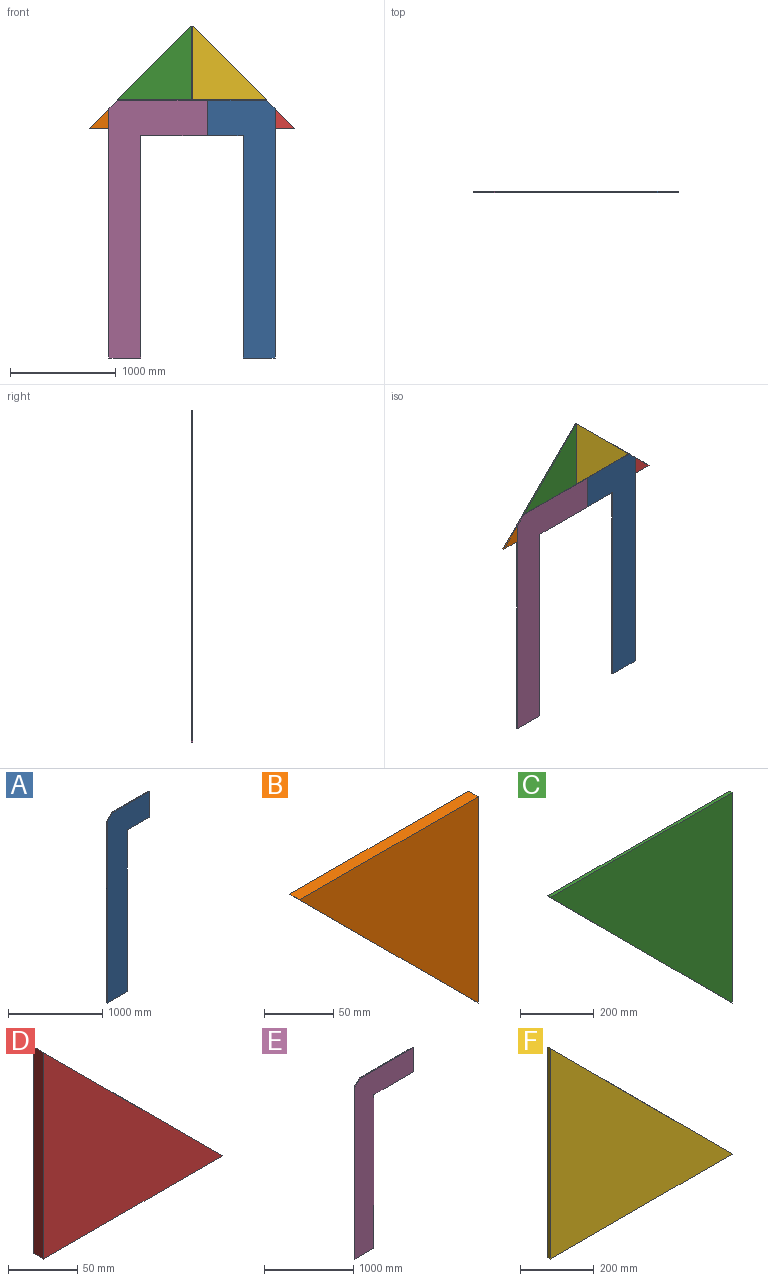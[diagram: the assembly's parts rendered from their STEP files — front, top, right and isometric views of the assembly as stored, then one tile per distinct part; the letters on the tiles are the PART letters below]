
ASSEMBLY  parts=6 mates=5
PART A: 9 faces, bbox 637.2x10.2x2435.2 mm
  f0: plane 2435.23x637.22mm, normal (0,-1,0), area 844527.8mm2, adj f1,f2,f3,f5,f6,f7,f8
  f1: plane 557.08x10.16mm, normal (0,0,1), area 5659.9mm2, adj f0,f4,f5,f8
  f2: plane 2355.08x10.16mm, normal (-1,0,0), area 23927.6mm2, adj f0,f3,f4,f8
  f3: plane 302.26x10.16mm, normal (0,0,-1), area 3071mm2, adj f0,f2,f4,f7
  f4: plane 2435.23x637.22mm, normal (0,1,0), area 844527.8mm2, adj f1,f2,f3,f5,f6,f7,f8
  f5: plane 333.38x10.16mm, normal (1,0,0), area 3387.1mm2, adj f0,f1,f4,f6
  f6: plane 334.96x10.16mm, normal (0,0,-1), area 3403.2mm2, adj f0,f4,f5,f7
  f7: plane 2101.85x10.16mm, normal (1,0,0), area 21354.8mm2, adj f0,f3,f4,f6
  f8: plane 80.14x80.14mm, normal (-0.71,0,0.71), area 1151.5mm2, adj f0,f1,f2,f4
PART B: 5 faces, bbox 182.9x10.2x182.9 mm
  f0: plane 182.88x10.16mm, normal (0,0,1), area 1858.1mm2, adj f1,f2,f3,f4
  f1: plane 182.88x182.88mm, normal (0,-1,0), area 16722.5mm2, adj f0,f3,f4
  f2: plane 182.88x182.88mm, normal (0,1,0), area 16722.5mm2, adj f0,f3,f4
  f3: plane 182.88x10.16mm, normal (1,0,0), area 1858.1mm2, adj f0,f1,f2,f4
  f4: plane 182.88x182.88mm, normal (-0.71,0,-0.71), area 2627.7mm2, adj f0,f1,f2,f3
PART C: 5 faces, bbox 698.5x10.2x700.1 mm
  f0: plane 700.09x10.16mm, normal (1,0,0), area 7112.9mm2, adj f1,f2,f3,f4
  f1: plane 700.09x698.5mm, normal (0,1,0), area 244505.6mm2, adj f0,f3,f4
  f2: plane 700.09x698.5mm, normal (0,-1,0), area 244505.6mm2, adj f0,f3,f4
  f3: plane 700.09x698.5mm, normal (-0.71,0,-0.71), area 10047.7mm2, adj f0,f1,f2,f4
  f4: plane 698.5x10.16mm, normal (0,0,1), area 7096.8mm2, adj f0,f1,f2,f3
PART D: 5 faces, bbox 182.9x10.2x182.9 mm
  f0: plane 182.88x182.88mm, normal (0,-1,0), area 16722.5mm2, adj f1,f3,f4
  f1: plane 182.88x10.16mm, normal (-1,0,0), area 1858.1mm2, adj f0,f2,f3,f4
  f2: plane 182.88x182.88mm, normal (0,1,0), area 16722.5mm2, adj f1,f3,f4
  f3: plane 182.88x182.88mm, normal (0.71,0,0.71), area 2627.7mm2, adj f0,f1,f2,f4
  f4: plane 182.88x10.16mm, normal (0,0,-1), area 1858.1mm2, adj f0,f1,f2,f3
PART E: 9 faces, bbox 929.3x10.2x2435.2 mm
  f0: plane 849.18x10.16mm, normal (0,0,1), area 8627.7mm2, adj f1,f2,f4,f8
  f1: plane 2435.23x929.32mm, normal (0,-1,0), area 933898.6mm2, adj f0,f3,f4,f5,f6,f7,f8
  f2: plane 2435.23x929.32mm, normal (0,1,0), area 933898.6mm2, adj f0,f3,f4,f5,f6,f7,f8
  f3: plane 298.45x10.16mm, normal (0,0,-1), area 3032.3mm2, adj f1,f2,f6,f7
  f4: plane 333.38x10.16mm, normal (1,0,0), area 3387.1mm2, adj f0,f1,f2,f5
  f5: plane 630.87x10.16mm, normal (0,0,-1), area 6409.7mm2, adj f1,f2,f4,f6
  f6: plane 2101.85x10.16mm, normal (1,0,0), area 21354.8mm2, adj f1,f2,f3,f5
  f7: plane 2355.08x10.16mm, normal (-1,0,0), area 23927.6mm2, adj f1,f2,f3,f8
  f8: plane 80.14x80.14mm, normal (-0.71,0,0.71), area 1151.5mm2, adj f0,f1,f2,f7
PART F: 5 faces, bbox 698.5x10.2x700.1 mm
  f0: plane 700.09x698.5mm, normal (0,-1,0), area 244505.6mm2, adj f2,f3,f4
  f1: plane 700.09x698.5mm, normal (0,1,0), area 244505.6mm2, adj f2,f3,f4
  f2: plane 698.5x10.16mm, normal (0,0,-1), area 7096.8mm2, adj f0,f1,f3,f4
  f3: plane 700.09x698.5mm, normal (0.71,0,0.71), area 10047.7mm2, adj f0,f1,f2,f4
  f4: plane 700.09x10.16mm, normal (-1,0,0), area 7112.9mm2, adj f0,f1,f2,f3
PLACE A rot(axis=(0,0,1),180deg) t=(-334.02,0,2435.23)mm
PLACE B rot(axis=(0,1,0),90deg) t=(73.02,10.16,2906.25)mm
PLACE C rot(axis=(0,1,0),90deg) t=(2509.55,10.16,442.58)mm
PLACE D t=(1018.55,10.16,2434.46)mm
PLACE E t=(3116.59,10.16,2435.23)mm
PLACE F rot(axis=(0.71,0,0.71),180deg) t=(3221.54,0,5132.72)mm
MATE fastened C.f2 <-> E.f1  axis (0,-1,0) through (83.32,0,2438.4)mm
MATE fastened E.f1 <-> A.f4  axis (0,-1,0) through (929.32,0,2435.23)mm
MATE fastened F.f1 <-> A.f4  axis (0,-1,0) through (1486.4,0,2438.4)mm
MATE fastened D.f0 <-> A.f4  axis (0,-1,0) through (1572.9,0,2351.91)mm
MATE fastened B.f1 <-> E.f1  axis (0,-1,0) through (-3.18,0,2351.91)mm
